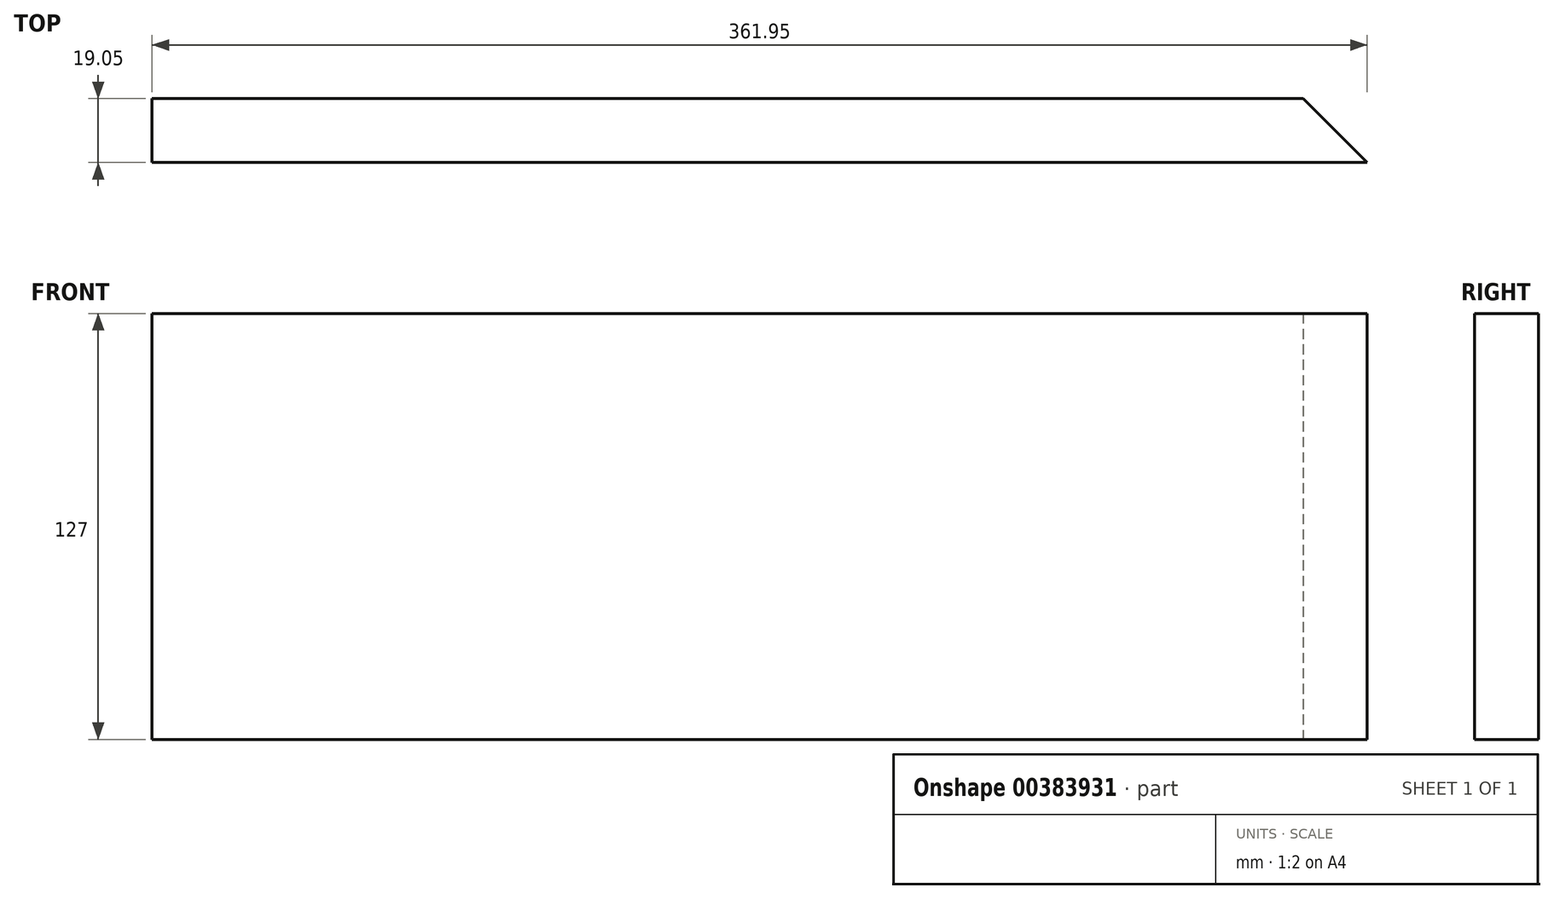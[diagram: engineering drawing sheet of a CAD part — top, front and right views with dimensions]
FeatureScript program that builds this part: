
annotation { "Feature Type Name" : "Feature", "Feature Type Description" : "" }
export const myFeature = defineFeature(function(context is Context, id is Id, definition is map)
    precondition{}
    {
        {
            var Q0;
            Q0=qCreatedBy(makeId("Front.planeOp"),FACE);
            var sketch = newSketch(context, id + "F0", { "sketchPlane" : qUnion([Q0])});
            skLineSegment(sketch, "E0.bottom", {"start": v(-151.36, 97.06) * mm, "end": v(210.59, 97.06) * mm});
            skLineSegment(sketch, "E0.top", {"start": v(-151.36, -29.94) * mm, "end": v(210.59, -29.94) * mm});
            skLineSegment(sketch, "E0.left", {"start": v(-151.36, 97.06) * mm, "end": v(-151.36, -29.94) * mm});
            skLineSegment(sketch, "E0.right", {"start": v(210.59, 97.06) * mm, "end": v(210.59, -29.94) * mm});
            skSolve(sketch);
        }
        {
            var Q0;
            Q0=makeQuery(id+"F0.imprint","IMPRINT",FACE,{"disambiguationData":[TD([[makeQuery(id+"F0.imprint","IMPRINT",EDGE,{"derivedFrom":sQuery(id+"F0.wireOp",EDGE,"E0.bottom")}),-1.0]])]});
            extrude(context, id + "F1", {"entities" : qUnion([Q0]), "depth" : 19.05 * mm});
        }
        {
            var Q0;
            Q0=makeQuery(id+"F1.opExtrude","CAP_EDGE",EDGE,{"disambiguationData":[OSD([sQuery(id+"F0.wireOp",EDGE,"E0.right")])],"isStart":true});
            chamfer(context, id + "F2", {"entities" : qUnion([Q0]), "chamferType" : ChamferType.OFFSET_ANGLE, "width" : 19.05 * mm, "oppositeDirection" : false, "angle" : 45 * degree, "tangentPropagation" : true});
        }
    });
